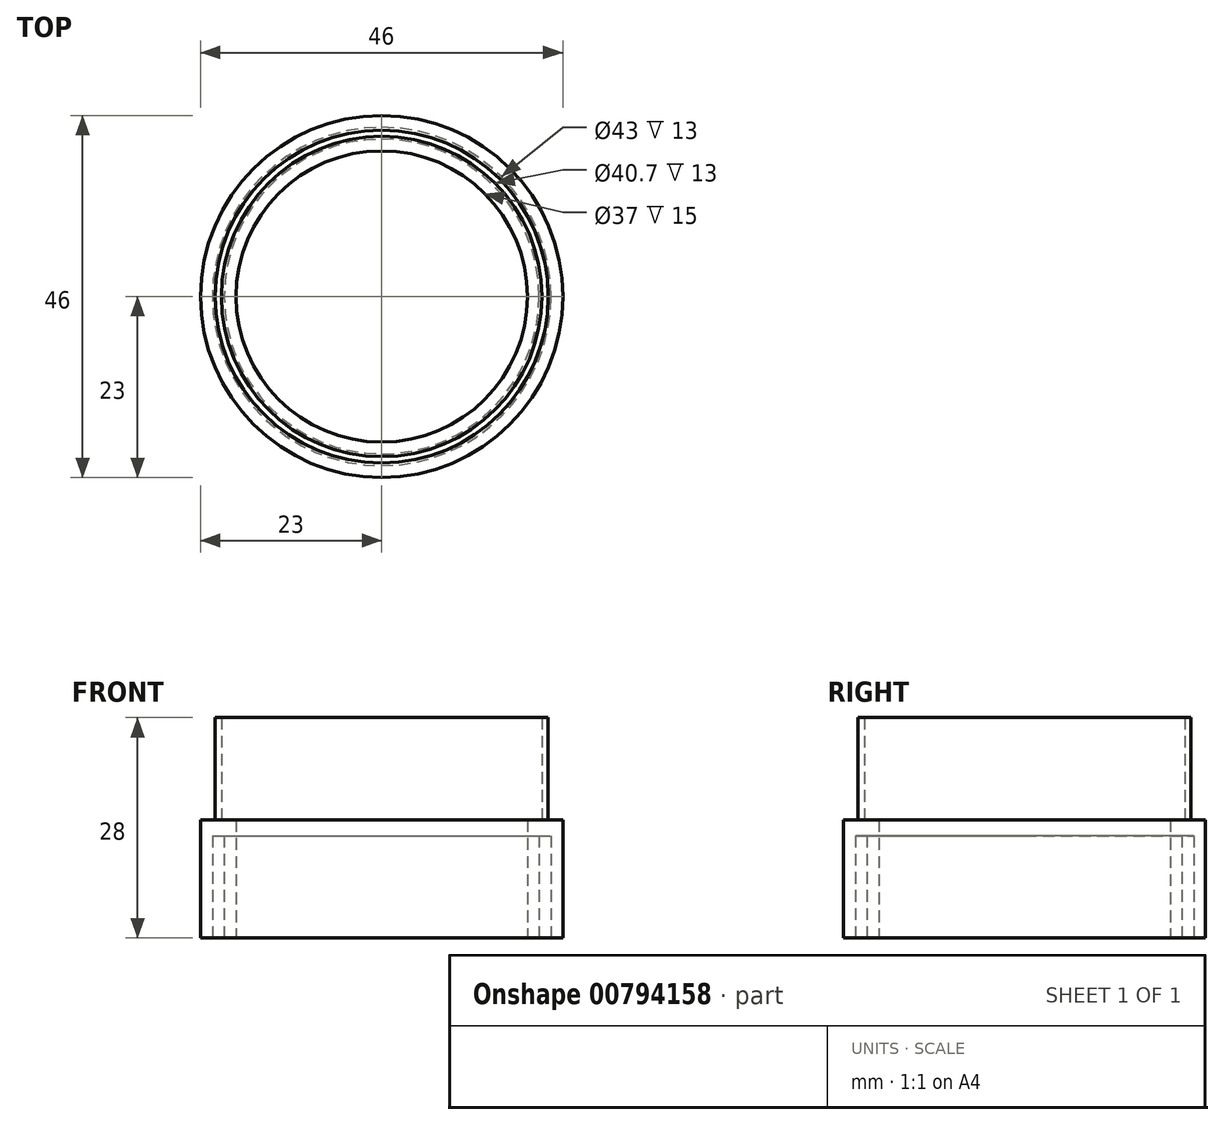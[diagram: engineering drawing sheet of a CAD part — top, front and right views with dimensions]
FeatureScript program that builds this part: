
annotation { "Feature Type Name" : "Feature", "Feature Type Description" : "" }
export const myFeature = defineFeature(function(context is Context, id is Id, definition is map)
    precondition{}
    {
        {
            var Q0;
            Q0=qCreatedBy(makeId("Front.planeOp"),FACE);
            var sketch = newSketch(context, id + "F0", { "sketchPlane" : qUnion([Q0])});
            skLineSegment(sketch, "E0.bottom", {"start": v(0, 0) * mm, "end": v(23, 0) * mm});
            skLineSegment(sketch, "E0.top", {"start": v(0, 15) * mm, "end": v(23, 15) * mm});
            skLineSegment(sketch, "E0.left", {"start": v(0, 0) * mm, "end": v(0, 15) * mm});
            skLineSegment(sketch, "E0.right", {"start": v(23, 0) * mm, "end": v(23, 15) * mm});
            skLineSegment(sketch, "E1.bottom", {"start": v(21.5, 15) * mm, "end": v(23, 15) * mm});
            skLineSegment(sketch, "E1.top", {"start": v(21.5, 0) * mm, "end": v(23, 0) * mm});
            skLineSegment(sketch, "E1.left", {"start": v(21.5, 15) * mm, "end": v(21.5, 0) * mm});
            skLineSegment(sketch, "E1.right", {"start": v(23, 15) * mm, "end": v(23, 0) * mm});
            skLineSegment(sketch, "E2.bottom", {"start": v(20, 15) * mm, "end": v(21.5, 15) * mm});
            skLineSegment(sketch, "E2.top", {"start": v(20, 0) * mm, "end": v(21.5, 0) * mm});
            skLineSegment(sketch, "E2.left", {"start": v(20, 15) * mm, "end": v(20, 0) * mm});
            skLineSegment(sketch, "E3.bottom", {"start": v(20, 15) * mm, "end": v(18.5, 15) * mm});
            skLineSegment(sketch, "E3.top", {"start": v(20, 0) * mm, "end": v(18.5, 0) * mm});
            skLineSegment(sketch, "E3.right", {"start": v(18.5, 15) * mm, "end": v(18.5, 0) * mm});
            skLineSegment(sketch, "E4.bottom", {"start": v(21.15, 15) * mm, "end": v(23, 15) * mm});
            skLineSegment(sketch, "E4.top", {"start": v(21.15, 28) * mm, "end": v(23, 28) * mm});
            skLineSegment(sketch, "E4.left", {"start": v(21.15, 15) * mm, "end": v(21.15, 28) * mm});
            skLineSegment(sketch, "E4.right", {"start": v(23, 15) * mm, "end": v(23, 28) * mm});
            skLineSegment(sketch, "E5.bottom", {"start": v(21.15, 15) * mm, "end": v(20.35, 15) * mm});
            skLineSegment(sketch, "E5.top", {"start": v(21.15, 28) * mm, "end": v(20.35, 28) * mm});
            skLineSegment(sketch, "E5.right", {"start": v(20.35, 15) * mm, "end": v(20.35, 28) * mm});
            skLineSegment(sketch, "E6.bottom", {"start": v(20.35, 28) * mm, "end": v(18.5, 28) * mm});
            skLineSegment(sketch, "E6.top", {"start": v(20.35, 15) * mm, "end": v(18.5, 15) * mm});
            skLineSegment(sketch, "E6.left", {"start": v(20.35, 28) * mm, "end": v(20.35, 15) * mm});
            skLineSegment(sketch, "E6.right", {"start": v(18.5, 28) * mm, "end": v(18.5, 15) * mm});
            skLineSegment(sketch, "E7.bottom", {"start": v(23, 15) * mm, "end": v(0, 15) * mm});
            skLineSegment(sketch, "E7.top", {"start": v(23, 13) * mm, "end": v(0, 13) * mm});
            skLineSegment(sketch, "E7.left", {"start": v(23, 15) * mm, "end": v(23, 13) * mm});
            skLineSegment(sketch, "E7.right", {"start": v(0, 15) * mm, "end": v(0, 13) * mm});
            skSolve(sketch);
        }
        {
            var Q0;
            {var subQ0=sQuery(id+"F0.wireOp",EDGE,"E3.right");var subQ1=sQuery(id+"F0.wireOp",EDGE,"E0.bottom");var subQ2=makeQuery(id+"F0.imprint","INTERSECT",VERTEX,{"derivedFrom":[subQ1,subQ0]});Q0=makeQuery(id+"F0.imprint","IMPRINT",FACE,{"disambiguationData":[TD([[makeQuery(id+"F0.imprint","IMPRINT",EDGE,{"disambiguationData":[TD([[subQ2,-1.0]])],"derivedFrom":subQ1}),1.0]])]});}
            var Q1;
            {var subQ0=sQuery(id+"F0.wireOp",EDGE,"E1.left");var subQ1=sQuery(id+"F0.wireOp",EDGE,"E0.bottom");var subQ2=makeQuery(id+"F0.imprint","INTERSECT",VERTEX,{"derivedFrom":[subQ1,subQ0]});Q1=makeQuery(id+"F0.imprint","IMPRINT",FACE,{"disambiguationData":[TD([[makeQuery(id+"F0.imprint","IMPRINT",EDGE,{"disambiguationData":[TD([[subQ2,-1.0]])],"derivedFrom":subQ1}),1.0]])]});}
            var Q2;
            {var subQ3=sQuery(id+"F0.wireOp",EDGE,"E1.left");var subQ5=sQuery(id+"F0.wireOp",EDGE,"E7.top");var subQ7=makeQuery(id+"F0.imprint","INTERSECT",VERTEX,{"derivedFrom":[subQ3,subQ5]});Q2=makeQuery(id+"F0.imprint","IMPRINT",FACE,{"disambiguationData":[TD([[makeQuery(id+"F0.imprint","IMPRINT",EDGE,{"disambiguationData":[TD([[subQ7,1.0]])],"derivedFrom":subQ3}),1.0]])]});}
            var Q3;
            {var subQ3=sQuery(id+"F0.wireOp",EDGE,"E0.top");var subQ5=makeQuery(id+"F0.imprint","INTERSECT",VERTEX,{"derivedFrom":[subQ3,sQuery(id+"F0.wireOp",EDGE,"E5.right")]});Q3=makeQuery(id+"F0.imprint","IMPRINT",FACE,{"disambiguationData":[TD([[makeQuery(id+"F0.imprint","IMPRINT",EDGE,{"disambiguationData":[TD([[subQ5,-1.0]])],"derivedFrom":subQ3}),-1.0]])]});}
            var Q4;
            {var subQ3=sQuery(id+"F0.wireOp",EDGE,"E2.left");var subQ5=sQuery(id+"F0.wireOp",EDGE,"E7.top");var subQ6=makeQuery(id+"F0.imprint","INTERSECT",VERTEX,{"derivedFrom":[subQ3,subQ5]});Q4=makeQuery(id+"F0.imprint","IMPRINT",FACE,{"disambiguationData":[TD([[makeQuery(id+"F0.imprint","IMPRINT",EDGE,{"disambiguationData":[TD([[subQ6,1.0]])],"derivedFrom":subQ3}),-1.0]])]});}
            var Q5;
            {var subQ2=sQuery(id+"F0.wireOp",EDGE,"E4.left");Q5=makeQuery(id+"F0.imprint","IMPRINT",FACE,{"disambiguationData":[TD([[makeQuery(id+"F0.imprint","IMPRINT",EDGE,{"derivedFrom":subQ2}),1.0]])]});}
            var Q6;
            Q6=sQuery(id+"F0.wireOp",EDGE,"E0.left");
            revolve(context, id + "F1", {"surfaceOperationType" : NewSurfaceOperationType.NEW, "entities" : qUnion([Q0, Q1, Q2, Q3, Q4, Q5]), "axis" : qUnion([Q6]), "revolveType" : RevolveType.FULL});
        }
    });
